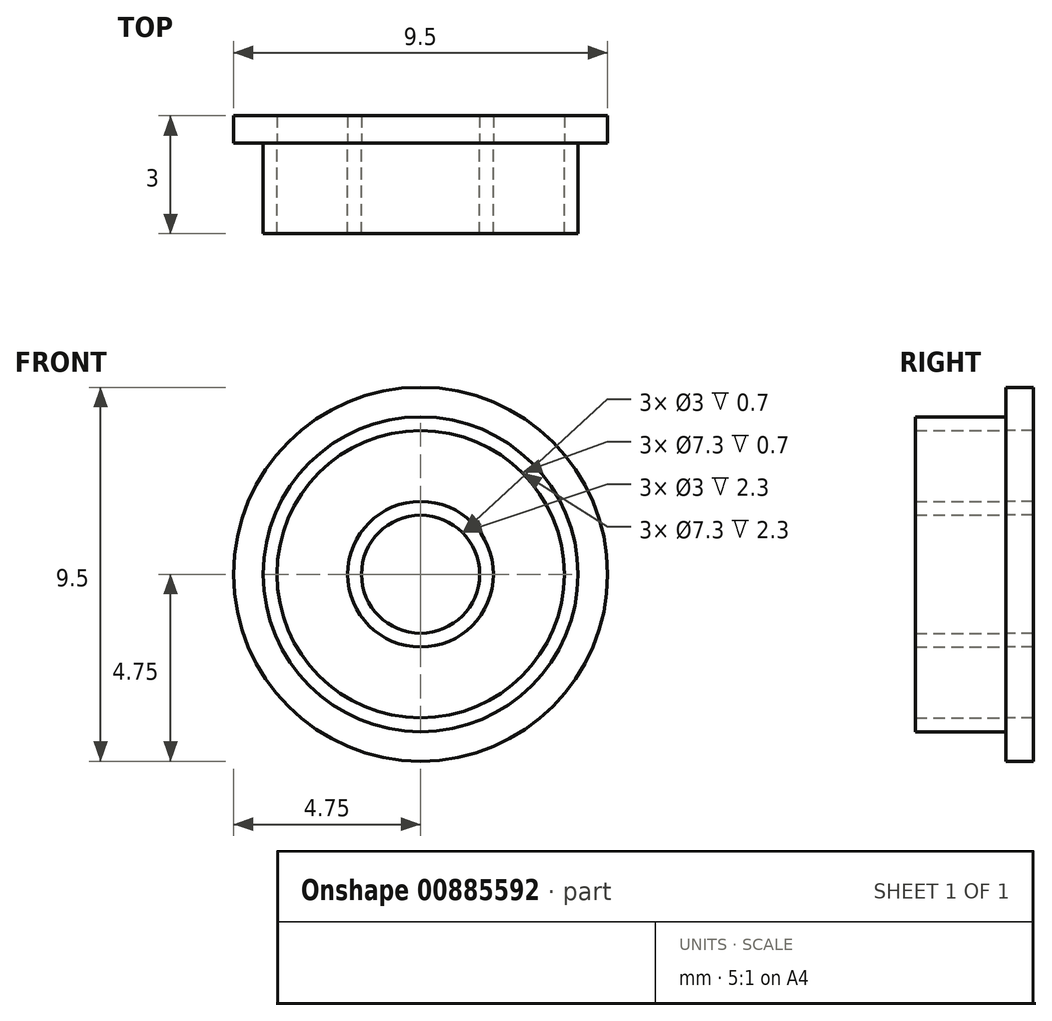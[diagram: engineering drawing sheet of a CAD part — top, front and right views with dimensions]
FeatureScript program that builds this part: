
annotation { "Feature Type Name" : "Feature", "Feature Type Description" : "" }
export const myFeature = defineFeature(function(context is Context, id is Id, definition is map)
    precondition{}
    {
        {
            var Q0;
            Q0=qCreatedBy(makeId("Front.planeOp"),FACE);
            var sketch = newSketch(context, id + "F0", { "sketchPlane" : qUnion([Q0])});
            skCircle(sketch, "E0", {"center": v(0, 0) * mm, "radius": 1.5 * mm});
            skCircle(sketch, "E1", {"center": v(0, 0) * mm, "radius": 1.85 * mm});
            skCircle(sketch, "E2", {"center": v(0, 0) * mm, "radius": 4 * mm});
            skCircle(sketch, "E3", {"center": v(0, 0) * mm, "radius": 3.65 * mm});
            skCircle(sketch, "E4", {"center": v(0, 0) * mm, "radius": 4.75 * mm});
            skSolve(sketch);
        }
        {
            var Q0;
            Q0=makeQuery(id+"F0.imprint","IMPRINT",FACE,{"disambiguationData":[TD([[makeQuery(id+"F0.imprint","IMPRINT",EDGE,{"derivedFrom":sQuery(id+"F0.wireOp",EDGE,"E2")}),1.0]])]});
            var Q1;
            Q1=makeQuery(id+"F0.imprint","IMPRINT",FACE,{"disambiguationData":[TD([[makeQuery(id+"F0.imprint","IMPRINT",EDGE,{"derivedFrom":sQuery(id+"F0.wireOp",EDGE,"E0")}),-1.0]])]});
            extrude(context, id + "F1", {"entities" : qUnion([Q0, Q1]), "depth" : 2.3 * mm, "offsetDistance" : 25 * mm});
        }
        {
            var Q0;
            Q0=makeQuery(id+"F0.imprint","IMPRINT",FACE,{"disambiguationData":[TD([[makeQuery(id+"F0.imprint","IMPRINT",EDGE,{"derivedFrom":sQuery(id+"F0.wireOp",EDGE,"E2")}),-1.0]])]});
            var Q1;
            Q1=makeQuery(id+"F0.imprint","IMPRINT",FACE,{"disambiguationData":[TD([[makeQuery(id+"F0.imprint","IMPRINT",EDGE,{"derivedFrom":sQuery(id+"F0.wireOp",EDGE,"E2")}),1.0]])]});
            var Q2;
            Q2=makeQuery(id+"F0.imprint","IMPRINT",FACE,{"disambiguationData":[TD([[makeQuery(id+"F0.imprint","IMPRINT",EDGE,{"derivedFrom":sQuery(id+"F0.wireOp",EDGE,"E0")}),-1.0]])]});
            extrude(context, id + "F2", {"entities" : qUnion([Q0, Q1, Q2]), "oppositeDirection" : true, "depth" : .7 * mm, "offsetDistance" : 25 * mm});
        }
    });
